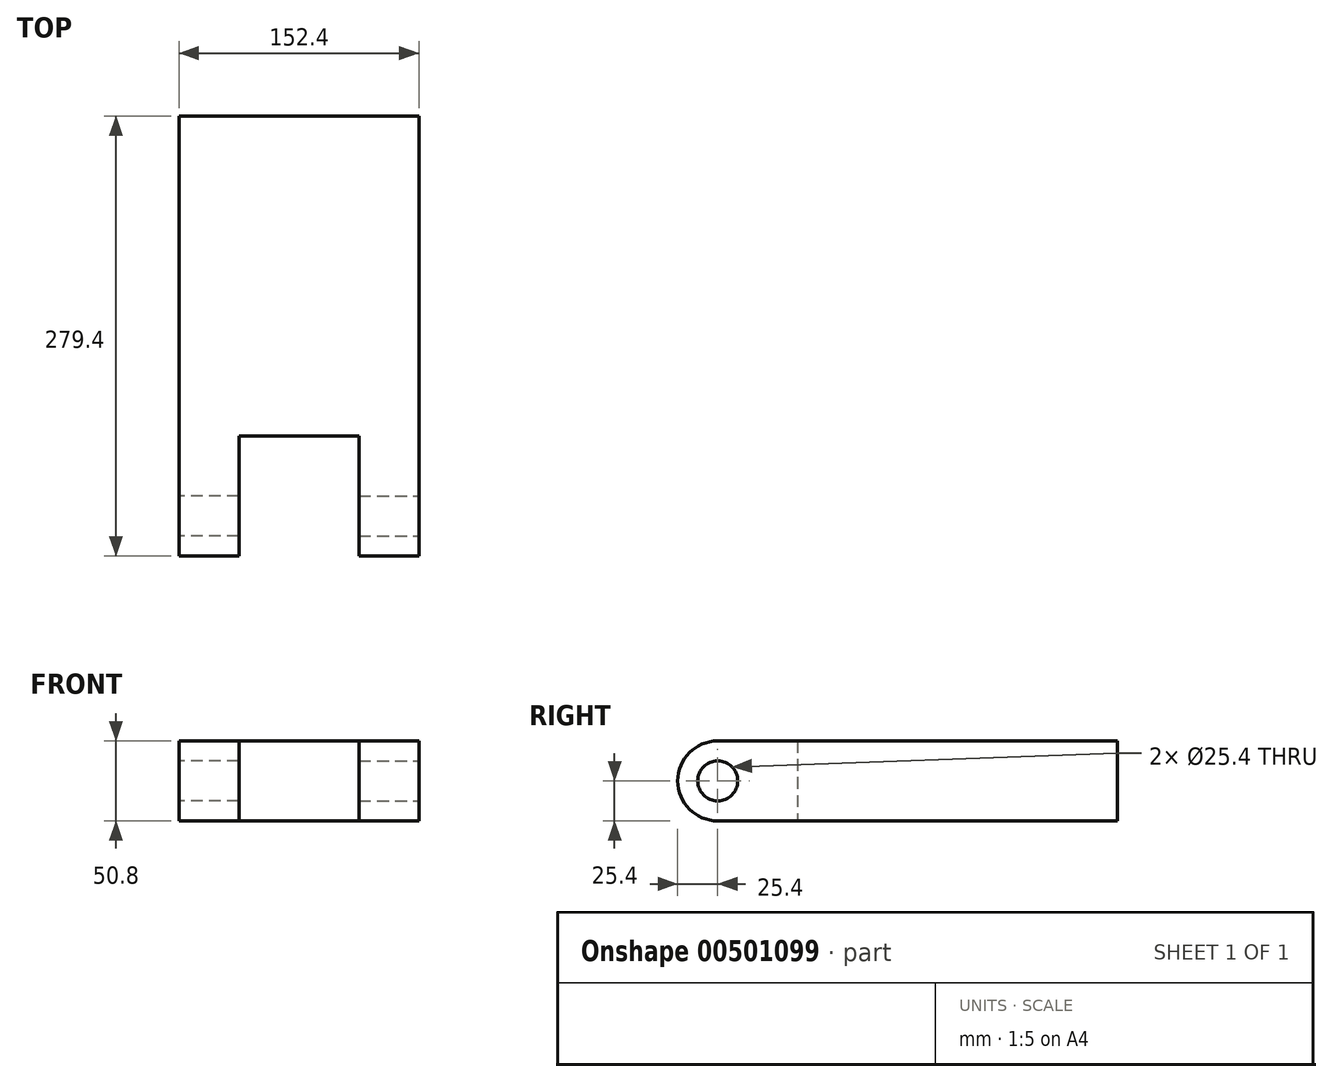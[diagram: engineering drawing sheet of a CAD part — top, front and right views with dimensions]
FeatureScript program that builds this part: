
annotation { "Feature Type Name" : "Feature", "Feature Type Description" : "" }
export const myFeature = defineFeature(function(context is Context, id is Id, definition is map)
    precondition{}
    {
        {
            var Q0;
            Q0=qCreatedBy(makeId("Top.planeOp"),FACE);
            var sketch = newSketch(context, id + "F0", { "sketchPlane" : qUnion([Q0])});
            skLineSegment(sketch, "E0.bottom", {"start": v(76.2, 101.6) * mm, "end": v(-76.2, 101.6) * mm});
            skLineSegment(sketch, "E0.top", {"start": v(38.1, -101.6) * mm, "end": v(-38.1, -101.6) * mm});
            skLineSegment(sketch, "E0.left", {"start": v(76.2, 101.6) * mm, "end": v(76.2, -101.6) * mm});
            skLineSegment(sketch, "E0.right", {"start": v(-76.2, 101.6) * mm, "end": v(-76.2, -101.6) * mm});
            skPoint(sketch, "E0.middle", {"position": v(0, 0) * mm});
            skLineSegment(sketch, "E1", {"start": v(-76.2, -101.6) * mm, "end": v(-76.2, -152.4) * mm});
            skLineSegment(sketch, "E2", {"start": v(-76.2, -152.4) * mm, "end": v(-38.1, -152.4) * mm});
            skLineSegment(sketch, "E3", {"start": v(-38.1, -152.4) * mm, "end": v(-38.1, -101.6) * mm});
            skLineSegment(sketch, "E4", {"start": v(76.2, -101.6) * mm, "end": v(76.2, -152.4) * mm});
            skLineSegment(sketch, "E5", {"start": v(76.2, -152.4) * mm, "end": v(38.1, -152.4) * mm});
            skLineSegment(sketch, "E6", {"start": v(38.1, -152.4) * mm, "end": v(38.1, -101.6) * mm});
            skSolve(sketch);
        }
        {
            var Q0;
            Q0=makeQuery(id+"F0.imprint","IMPRINT",FACE,{"disambiguationData":[TD([[makeQuery(id+"F0.imprint","IMPRINT",EDGE,{"derivedFrom":sQuery(id+"F0.wireOp",EDGE,"E0.bottom")}),1.0]])]});
            extrude(context, id + "F1", {"entities" : qUnion([Q0]), "endBound" : BoundingType.SYMMETRIC, "depth" : 50.8 * mm});
        }
        {
            var Q0;
            Q0=makeQuery(id+"F1.opExtrude","SWEPT_FACE",FACE,{"disambiguationData":[OSD([sQuery(id+"F0.wireOp",EDGE,"E0.right"),sQuery(id+"F0.wireOp",EDGE,"E1")])]});
            var sketch = newSketch(context, id + "F2", { "sketchPlane" : qUnion([Q0])});
            skArc(sketch, "E7", {"start": v(152.4, -25.4) * mm, "mid": v(177.8, 0) * mm, "end": v(152.4, 25.4) * mm});
            skArc(sketch, "E8", {"start": v(152.4, -12.7) * mm, "mid": v(165.1, 0) * mm, "end": v(152.4, 12.7) * mm});
            skLineSegment(sketch, "E9", {"start": v(152.4, -25.4) * mm, "end": v(152.4, -12.7) * mm});
            skLineSegment(sketch, "E10", {"start": v(152.4, 25.4) * mm, "end": v(152.4, 12.7) * mm});
            skSolve(sketch);
        }
        {
            var Q0;
            Q0=makeQuery(id+"F2.imprint","IMPRINT",FACE,{"disambiguationData":[TD([[makeQuery(id+"F2.imprint","IMPRINT",EDGE,{"derivedFrom":sQuery(id+"F2.wireOp",EDGE,"E7")}),1.0]])]});
            extrude(context, id + "F3", {"entities" : qUnion([Q0]), "operationType" : NewBodyOperationType.ADD, "oppositeDirection" : true, "depth" : 38.1 * mm});
        }
        {
            var Q0;
            Q0=makeQuery(id+"F1.opExtrude","SWEPT_FACE",FACE,{"disambiguationData":[OSD([sQuery(id+"F0.wireOp",EDGE,"E0.left"),sQuery(id+"F0.wireOp",EDGE,"E4")])]});
            var sketch = newSketch(context, id + "F4", { "sketchPlane" : qUnion([Q0])});
            skArc(sketch, "E11", {"start": v(-152.4, 25.4) * mm, "mid": v(-177.8, 0) * mm, "end": v(-152.4, -25.4) * mm});
            skArc(sketch, "E12", {"start": v(-152.4, 12.7) * mm, "mid": v(-165.1, 0) * mm, "end": v(-152.4, -12.7) * mm});
            skLineSegment(sketch, "E13", {"start": v(-152.4, 25.4) * mm, "end": v(-152.4, 12.7) * mm});
            skLineSegment(sketch, "E14", {"start": v(-152.4, -25.4) * mm, "end": v(-152.4, -12.7) * mm});
            skSolve(sketch);
        }
        {
            var Q0;
            Q0=makeQuery(id+"F4.imprint","IMPRINT",FACE,{"disambiguationData":[TD([[makeQuery(id+"F4.imprint","IMPRINT",EDGE,{"derivedFrom":sQuery(id+"F4.wireOp",EDGE,"E11")}),1.0]])]});
            extrude(context, id + "F5", {"entities" : qUnion([Q0]), "operationType" : NewBodyOperationType.ADD, "oppositeDirection" : true, "depth" : 38.1 * mm});
        }
        {
            var Q0;
            Q0=makeQuery(id+"F3.boolean.opBoolean","MERGE",FACE,{"derivedFrom":[makeQuery(id+"F1.opExtrude","SWEPT_FACE",FACE,{"disambiguationData":[OSD([sQuery(id+"F0.wireOp",EDGE,"E0.right"),sQuery(id+"F0.wireOp",EDGE,"E1")])]}),makeQuery(id+"F3.opExtrude","CAP_FACE",FACE,{"disambiguationData":[OSD([sQuery(id+"F2.wireOp",EDGE,"E7"),sQuery(id+"F2.wireOp",EDGE,"E8"),sQuery(id+"F2.wireOp",EDGE,"E9"),sQuery(id+"F2.wireOp",EDGE,"E10")])],"isStart":true})]});
            var sketch = newSketch(context, id + "F6", { "sketchPlane" : qUnion([Q0])});
            skCircle(sketch, "E15", {"center": v(152.4, 0) * mm, "radius": 12.7 * mm});
            skSolve(sketch);
        }
        {
            var Q0;
            Q0=sQuery(id+"F6.wireOp",VERTEX,"E15.center");
            var Q1;
            Q1=makeQuery(id+"F1.opExtrude","SWEPT_BODY",BODY,{"disambiguationData":[OSD([sQuery(id+"F0.wireOp",EDGE,"E0.bottom"),sQuery(id+"F0.wireOp",EDGE,"E0.top"),sQuery(id+"F0.wireOp",EDGE,"E0.left"),sQuery(id+"F0.wireOp",EDGE,"E0.right"),sQuery(id+"F0.wireOp",EDGE,"E1"),sQuery(id+"F0.wireOp",EDGE,"E2"),sQuery(id+"F0.wireOp",EDGE,"E3"),sQuery(id+"F0.wireOp",EDGE,"E4"),sQuery(id+"F0.wireOp",EDGE,"E5"),sQuery(id+"F0.wireOp",EDGE,"E6")])]});
            hole(context, id + "F7", {"style" : HoleStyle.SIMPLE, "endStyle" : HoleEndStyle.THROUGH, "holeDiameter" : 25.4 * mm, "isTappedThrough" : true, "tappedDepth" : 12.7 * mm, "tapClearance" : 3, "locations" : qUnion([Q0]), "scope" : qUnion([Q1])});
        }
    });
